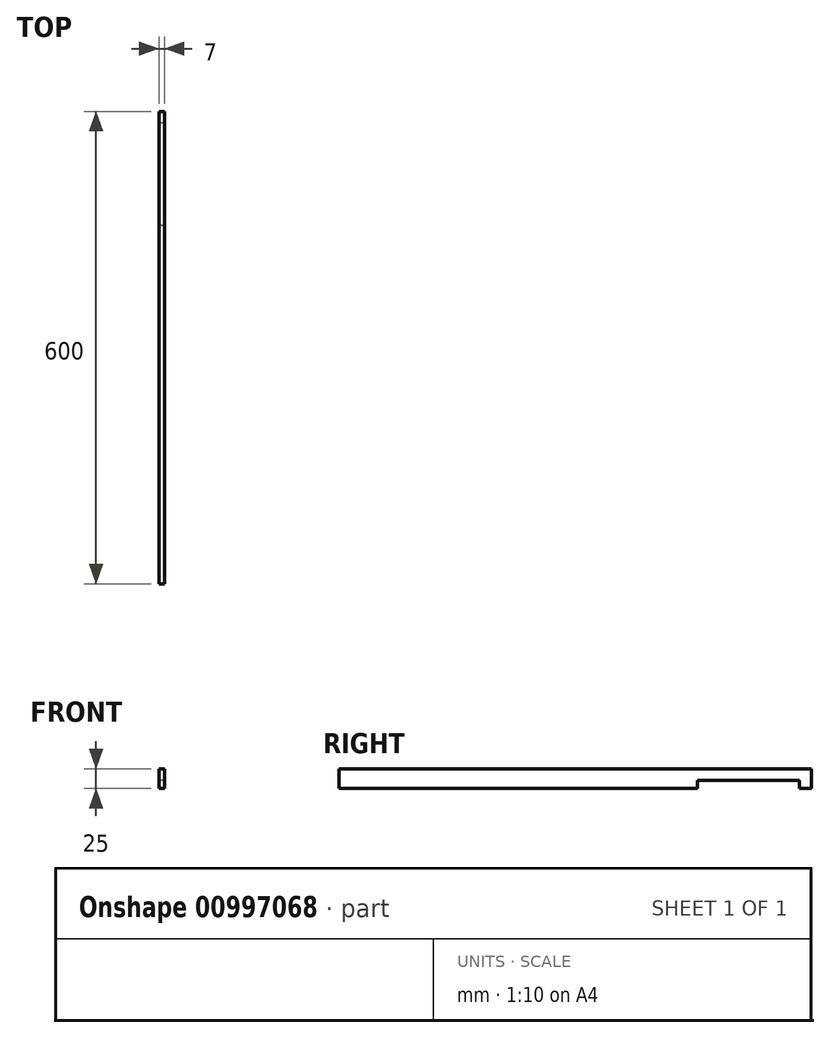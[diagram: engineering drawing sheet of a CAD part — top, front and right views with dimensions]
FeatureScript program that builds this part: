
annotation { "Feature Type Name" : "Feature", "Feature Type Description" : "" }
export const myFeature = defineFeature(function(context is Context, id is Id, definition is map)
    precondition{}
    {
        {
            var Q0;
            Q0=qCreatedBy(makeId("Right.planeOp"),FACE);
            var sketch = newSketch(context, id + "F0", { "sketchPlane" : qUnion([Q0])});
            skLineSegment(sketch, "E0", {"start": v(0, 0) * mm, "end": v(0, 25) * mm});
            skLineSegment(sketch, "E1", {"start": v(0, 25) * mm, "end": v(-600, 25) * mm});
            skLineSegment(sketch, "E2", {"start": v(-600, 25) * mm, "end": v(-600, 0) * mm});
            skLineSegment(sketch, "E3", {"start": v(-600, 0) * mm, "end": v(-145, 0) * mm});
            skLineSegment(sketch, "E4", {"start": v(-145, 0) * mm, "end": v(-145, 10) * mm});
            skLineSegment(sketch, "E5", {"start": v(-145, 10) * mm, "end": v(-15, 10) * mm});
            skLineSegment(sketch, "E6", {"start": v(-15, 10) * mm, "end": v(-15, 0) * mm});
            skLineSegment(sketch, "E7", {"start": v(-15, 0) * mm, "end": v(0, 0) * mm});
            skSolve(sketch);
        }
        {
            var Q0;
            Q0 = qSketchRegion(id + "F0", true);
            extrude(context, id + "F1", {"entities" : qUnion([Q0]), "depth" : 7 * mm, "offsetDistance" : 25 * mm});
        }
    });
